# Revit family: Hager-VOLTA-Surface_mounted-IP30-Without_Cover-With_DIN-Hosted-NL-en
name_source: partatom
category: Electrical Equipment
units: mm (PartAtom-declared; Revit-internal decimal feet)

## family parameters
Cut with Voids When Loaded = No
Host = Face
Maintain Annotation Orientation = Yes
Panel Configuration = Two Columns, Circuits Across
Part Type = Panelboard
Room Calculation Point = No
Round Connector Dimension = Use Diameter
Shared = No

## types (4) — shared parameters
BC_MODEL_ID = 1547207
BC_OBJECT_ID = 513495
BC_OBJECT_VERSION = #3
Code hager = ADD-EC000214_EU
EF000003 - Mounting method = Surface mounted
EF000007 - Colour = White
EF000024 - UV resistant = No
EF000049 - Depth = 96 mm  [stored 0.314961 ft]
EF000116 - RAL-number = 9010
EF000118 - With mounting plate = No
EF001062 - EMC-version = No
EF001088 - Extension possible = Yes
EF001134 - DIN-rail = Yes
EF002950 - Width in number of modular spacings = 12
EF005474 - Degree of protection (IP) = IP30
EF006244 - Transparent cover/door = No
EF006306 - With lock = No
EF009212 - Cover model = With notch
EF015776 - Earthing terminal block = Yes
EF015777 - Neutral terminal block = Yes
EF015941 - Signal passing door = No
ETIM class code = EC000214
ETIM class name = Small distribution board
HG000001-Number of columns = 1
HG000002-With door or cover = No
HG000003-Range = VOLTA
HG000005-Thickness = 2 mm  [stored 0.00656168 ft]
HG000006-Flush mounted = No
HG000009-Double swing door = No
HG000010-Asymmetric doors = No
HG000011-Empty rows from bottom = No
HG000012-Door swing angle = 90.00°
HG000013-Door on the left = No
HG000014-Door on the right = Yes
HG000015-Clearance visibility = Yes
HG000016-Door 3D visibility = Yes
HG000017-Distance between poles = 18 mm  [stored 0.0590551 ft]
HG000060-RAL-number = 9010
HG000099-Onfly Template ID = 507532
HGEF002950-Width in number of modular spacings = 12
Manufacturer = Hager
Name = VOLTA-Surface_mounted-IP30-Without_Cover-With_DIN-NL
Name BIM&CO = Electricity
Name hager = ADD_Enclosures_EC000214
Uniformat = Low Tension Service & Dist.
Uniformat code = D501001
zero-valued in all types: Default Elevation, EF000218 - Built-in depth, EF000332 - Built-in height, EF000846 - Built-in width, EF001131 - Inner depth, HG000007-Number of empty columns, HG000008-Number of empty rows

## per-type parameters (varying)
| type | BC_VARIANT_ID | EF000008 - Width | EF000040 - Height | EF000266 - Number of rows | HG000004-Manufacturer reference | HGEF000266-Number of rows |
| VOLTA-Surface_mounted_W348_H245_D96_12_Modular_Spacing-VA12NL | 1174365 | 348 mm  [stored 1.14173 ft] | 245 mm  [stored 0.803806 ft] | 1 | VA12NL | 1 |
| VOLTA-Surface_mounted_W305_H370_D96_12_Modular_Spacing-VA24NL | 1174366 | 305 mm  [stored 1.00066 ft] | 370 mm  [stored 1.21391 ft] | 2 | VA24NL | 2 |
| VOLTA-Surface_mounted_W305_H515_D96_12_Modular_Spacing-VA36NL | 1174368 | 305 mm  [stored 1.00066 ft] | 515 mm  [stored 1.68963 ft] | 3 | VA36NL | 3 |
| VOLTA-Surface_mounted_W305_H640_D96_12_Modular_Spacing-VA48NL | 1174370 | 305 mm  [stored 1.00066 ft] | 640 mm  [stored 2.09974 ft] | 4 | VA48NL | 4 |

note: column(s) folded — value = type name in every type: Reference

note: [stored X ft] marks values corroborated as IEEE doubles in the binary element streams (Revit-internal decimal feet)

## geometry (parser evidence)
native form markers: Sweep x14
no freeform markers — native parametric forms only
